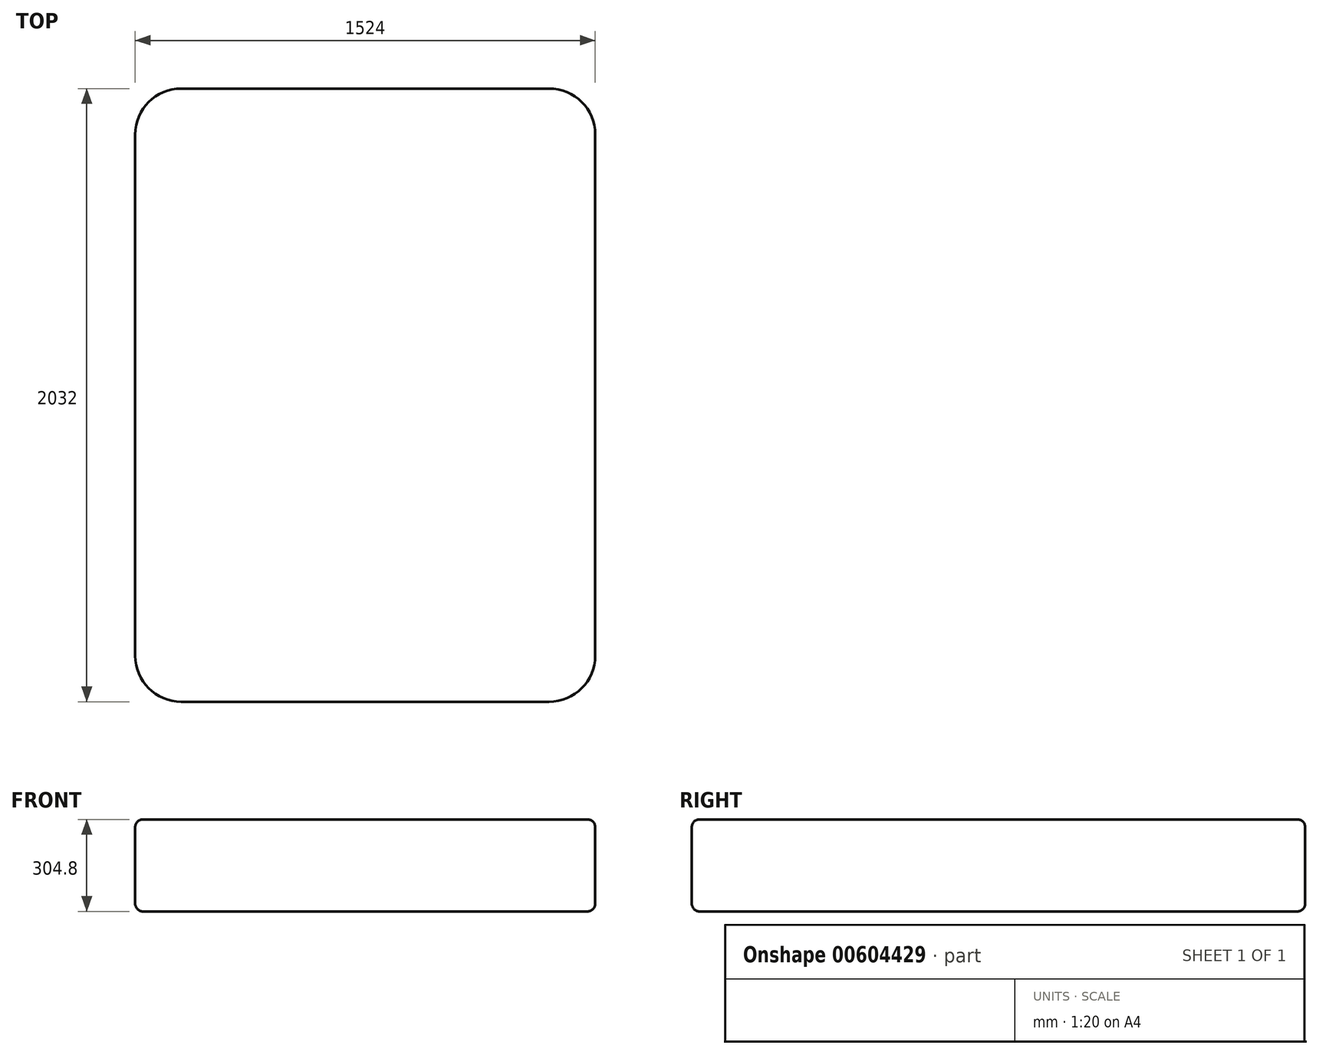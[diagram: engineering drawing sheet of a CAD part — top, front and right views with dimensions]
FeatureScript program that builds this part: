
annotation { "Feature Type Name" : "Feature", "Feature Type Description" : "" }
export const myFeature = defineFeature(function(context is Context, id is Id, definition is map)
    precondition{}
    {
        {
            var Q0;
            Q0=qCreatedBy(makeId("Top.planeOp"),FACE);
            var sketch = newSketch(context, id + "F0", { "sketchPlane" : qUnion([Q0])});
            skLineSegment(sketch, "E0.bottom", {"start": v(-762, 1016) * mm, "end": v(762, 1016) * mm});
            skLineSegment(sketch, "E0.top", {"start": v(-762, -1016) * mm, "end": v(762, -1016) * mm});
            skLineSegment(sketch, "E0.left", {"start": v(-762, 1016) * mm, "end": v(-762, -1016) * mm});
            skLineSegment(sketch, "E0.right", {"start": v(762, 1016) * mm, "end": v(762, -1016) * mm});
            skLineSegment(sketch, "E1", {"start": v(0, 1016) * mm, "end": v(0, -1016) * mm, "construction": true});
            skLineSegment(sketch, "E2", {"start": v(-762, 0) * mm, "end": v(762, 0) * mm, "construction": true});
            skSolve(sketch);
        }
        {
            var Q0;
            Q0 = qSketchRegion(id + "F0", true);
            extrude(context, id + "F1", {"entities" : qUnion([Q0]), "depth" : 304.8 * mm, "offsetDistance" : 25.4 * mm});
        }
        {
            var Q0;
            Q0=makeQuery(id+"F1.opExtrude","SWEPT_EDGE",EDGE,{"disambiguationData":[OSD([sQuery(id+"F0.wireOp",EDGE,"E0.top"),sQuery(id+"F0.wireOp",EDGE,"E0.left")])]});
            var Q1;
            Q1=makeQuery(id+"F1.opExtrude","SWEPT_EDGE",EDGE,{"disambiguationData":[OSD([sQuery(id+"F0.wireOp",EDGE,"E0.top"),sQuery(id+"F0.wireOp",EDGE,"E0.right")])]});
            var Q2;
            Q2=makeQuery(id+"F1.opExtrude","SWEPT_EDGE",EDGE,{"disambiguationData":[OSD([sQuery(id+"F0.wireOp",EDGE,"E0.bottom"),sQuery(id+"F0.wireOp",EDGE,"E0.right")])]});
            var Q3;
            Q3=makeQuery(id+"F1.opExtrude","SWEPT_EDGE",EDGE,{"disambiguationData":[OSD([sQuery(id+"F0.wireOp",EDGE,"E0.bottom"),sQuery(id+"F0.wireOp",EDGE,"E0.left")])]});
            fillet(context, id + "F2", {"entities" : qUnion([Q0, Q1, Q2, Q3]), "radius" : 152.4 * mm, "tangentPropagation" : true, "allowEdgeOverflow" : false});
        }
        {
            var Q0;
            Q0=makeQuery(id+"F1.opExtrude","CAP_FACE",FACE,{"disambiguationData":[OSD([sQuery(id+"F0.wireOp",EDGE,"E0.bottom"),sQuery(id+"F0.wireOp",EDGE,"E0.top"),sQuery(id+"F0.wireOp",EDGE,"E0.left"),sQuery(id+"F0.wireOp",EDGE,"E0.right")])],"isStart":false});
            var Q1;
            Q1=makeQuery(id+"F1.opExtrude","CAP_FACE",FACE,{"disambiguationData":[OSD([sQuery(id+"F0.wireOp",EDGE,"E0.bottom"),sQuery(id+"F0.wireOp",EDGE,"E0.top"),sQuery(id+"F0.wireOp",EDGE,"E0.left"),sQuery(id+"F0.wireOp",EDGE,"E0.right")])],"isStart":true});
            fillet(context, id + "F3", {"entities" : qUnion([Q0, Q1]), "radius" : 25.4 * mm, "tangentPropagation" : true, "allowEdgeOverflow" : false});
        }
    });
